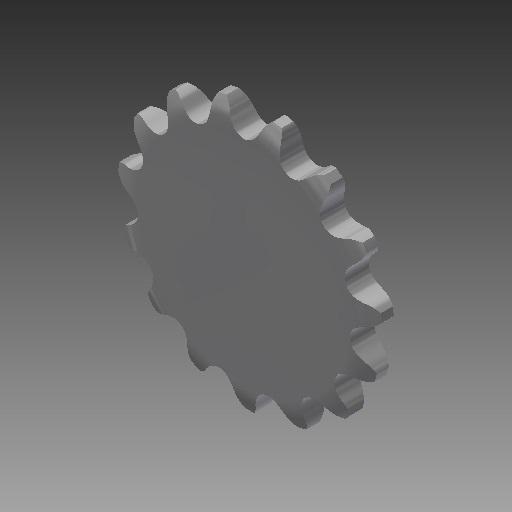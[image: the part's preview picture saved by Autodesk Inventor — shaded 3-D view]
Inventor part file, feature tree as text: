
AUTODESK INVENTOR PART (.ipt)
format: ipt  version: 2017 (Build 210142000, 142)  size: 505,856 bytes
history: native  units: mm
features: other x6, extrude x2, pattern_linear x1, pattern_circular x1
ambient origin geometry x8: Origin, YZ Plane, XZ Plane, XY Plane, X Axis, Y Axis, Z Axis, Center Point
bodies: Solid1 (feature_tree)
feature tree (10):
  other  "Theoretical Tooth Profile"
  other  "Tooth Profile"
  other  "Section Profile"
  other  "Shroud"
  other  "Strand"
  pattern_linear  "Strand Pattern"  Spacing1=30.541813mm  [1 undecoded]
  extrude  "Theoretical Tooth"  Depth=4.18879mm
  extrude  "Tooth"  Depth=1.697355mm
  pattern_circular  "Tooth Pattern"  [2 undecoded]
  other  "Timing Plane"
note: 3 required parameter values undecoded (feature->parameter linkage not recoverable at this tier; creation-order binding heuristic only, values carry confidence <= 0.55)
